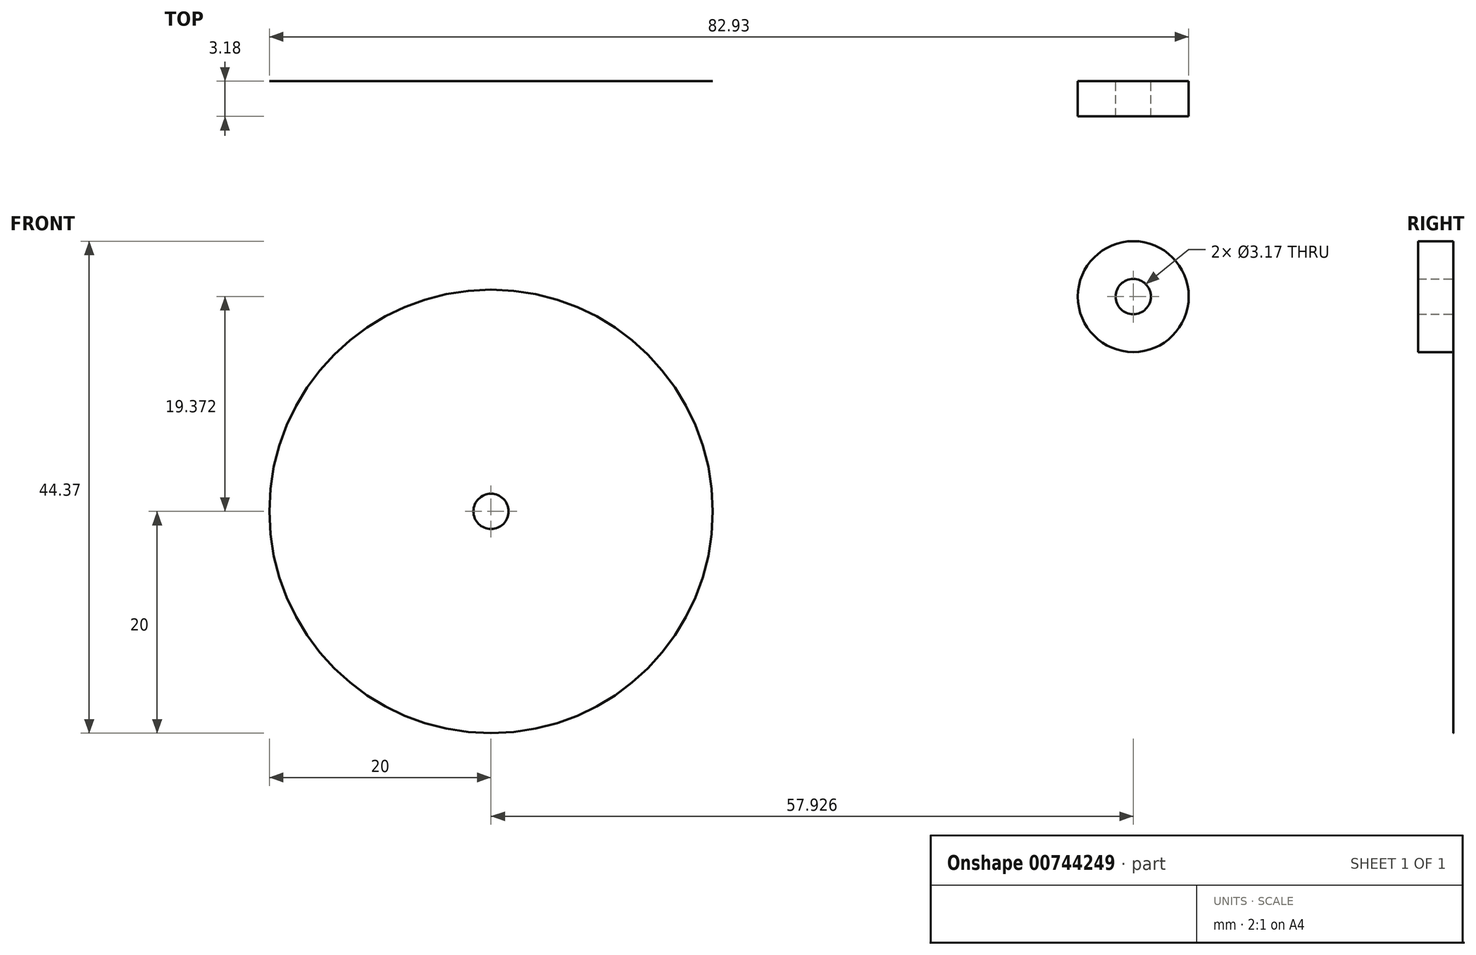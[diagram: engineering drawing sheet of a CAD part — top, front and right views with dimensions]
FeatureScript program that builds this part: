
annotation { "Feature Type Name" : "Feature", "Feature Type Description" : "" }
export const myFeature = defineFeature(function(context is Context, id is Id, definition is map)
    precondition{}
    {
        {
            var Q0;
            Q0=qCreatedBy(makeId("Front.planeOp"),FACE);
            var sketch = newSketch(context, id + "F0", { "sketchPlane" : qUnion([Q0])});
            skCircle(sketch, "E0", {"center": v(0, 0) * mm, "radius": 20 * mm});
            skCircle(sketch, "E1", {"center": v(0, 0) * mm, "radius": 1.59 * mm});
            skSolve(sketch);
        }
        {
            var Q0;
            Q0 = qSketchRegion(id + "F0", true);
            extrude(context, id + "F1", {"entities" : qUnion([Q0]), "depth" : 1 / 203.2 * mm, "offsetDistance" : 25.4 * mm});
        }
        {
            var Q0;
            Q0=qCreatedBy(makeId("Front.planeOp"),FACE);
            var sketch = newSketch(context, id + "F2", { "sketchPlane" : qUnion([Q0])});
            skCircle(sketch, "E2", {"center": v(57.93, 19.37) * mm, "radius": 5 * mm});
            skCircle(sketch, "E3", {"center": v(57.93, 19.37) * mm, "radius": 1.59 * mm});
            skSolve(sketch);
        }
        {
            var Q0;
            Q0 = qSketchRegion(id + "F2", true);
            extrude(context, id + "F3", {"entities" : qUnion([Q0]), "depth" : 3.17 * mm, "offsetDistance" : 25.4 * mm});
        }
    });
